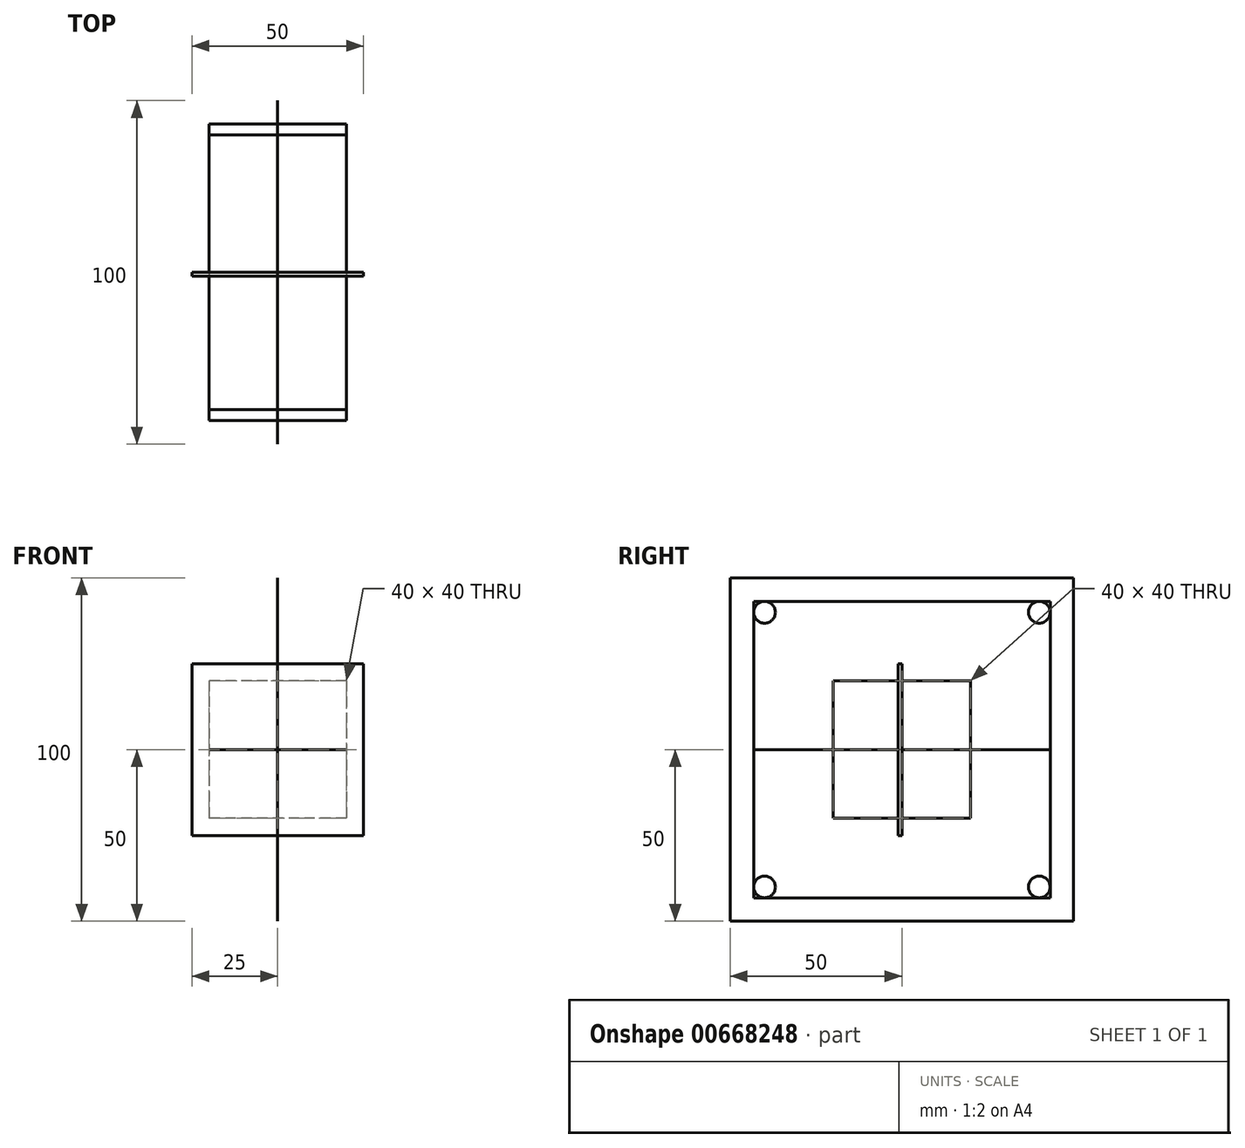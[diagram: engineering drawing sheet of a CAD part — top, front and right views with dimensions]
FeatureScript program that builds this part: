
annotation { "Feature Type Name" : "Feature", "Feature Type Description" : "" }
export const myFeature = defineFeature(function(context is Context, id is Id, definition is map)
    precondition{}
    {
        {
            var Q0;
            Q0=qCreatedBy(makeId("Front.planeOp"),FACE);
            var sketch = newSketch(context, id + "F0", { "sketchPlane" : qUnion([Q0])});
            skLineSegment(sketch, "E0.bottom", {"start": v(25, 25) * mm, "end": v(-25, 25) * mm});
            skLineSegment(sketch, "E0.top", {"start": v(25, -25) * mm, "end": v(-25, -25) * mm});
            skLineSegment(sketch, "E0.left", {"start": v(25, 25) * mm, "end": v(25, -25) * mm});
            skLineSegment(sketch, "E0.right", {"start": v(-25, 25) * mm, "end": v(-25, -25) * mm});
            skPoint(sketch, "E0.middle", {"position": v(0, 0) * mm});
            skLineSegment(sketch, "E1.bottom", {"start": v(20, 20) * mm, "end": v(-20, 20) * mm});
            skLineSegment(sketch, "E1.top", {"start": v(20, -20) * mm, "end": v(-20, -20) * mm});
            skLineSegment(sketch, "E1.left", {"start": v(20, 20) * mm, "end": v(20, -20) * mm});
            skLineSegment(sketch, "E1.right", {"start": v(-20, 20) * mm, "end": v(-20, -20) * mm});
            skSolve(sketch);
        }
        {
            var Q0;
            Q0=makeQuery(id+"F0.imprint","IMPRINT",FACE,{"disambiguationData":[TD([[makeQuery(id+"F0.imprint","IMPRINT",EDGE,{"derivedFrom":sQuery(id+"F0.wireOp",EDGE,"E0.bottom")}),1.0]])]});
            extrude(context, id + "F1", {"entities" : qUnion([Q0]), "depth" : 1 / 406.4 * mm, "offsetDistance" : 25.4 * mm});
        }
        {
            var Q0;
            Q0=qCreatedBy(makeId("Right.planeOp"),FACE);
            var sketch = newSketch(context, id + "F2", { "sketchPlane" : qUnion([Q0])});
            skLineSegment(sketch, "E2.bottom", {"start": v(-20, 20) * mm, "end": v(20, 20) * mm});
            skLineSegment(sketch, "E2.top", {"start": v(-20, -20) * mm, "end": v(20, -20) * mm});
            skLineSegment(sketch, "E2.left", {"start": v(-20, 20) * mm, "end": v(-20, -20) * mm});
            skLineSegment(sketch, "E2.right", {"start": v(20, 20) * mm, "end": v(20, -20) * mm});
            skPoint(sketch, "E2.middle", {"position": v(0, 0) * mm});
            skLineSegment(sketch, "E3.bottom", {"start": v(-50, 50) * mm, "end": v(50, 50) * mm});
            skLineSegment(sketch, "E3.top", {"start": v(-50, -50) * mm, "end": v(50, -50) * mm});
            skLineSegment(sketch, "E3.left", {"start": v(-50, 50) * mm, "end": v(-50, -50) * mm});
            skLineSegment(sketch, "E3.right", {"start": v(50, 50) * mm, "end": v(50, -50) * mm});
            skCircle(sketch, "E4", {"center": v(-40, 40) * mm, "radius": 3.18 * mm});
            skLineSegment(sketch, "E5", {"start": v(-20, 20) * mm, "end": v(-50, 50) * mm, "construction": true});
            skCircle(sketch, "E6.1.0", {"center": v(-40, -40) * mm, "radius": 3.18 * mm});
            skCircle(sketch, "E6.2.0", {"center": v(40, -40) * mm, "radius": 3.18 * mm});
            skCircle(sketch, "E6.3.0", {"center": v(40, 40) * mm, "radius": 3.18 * mm});
            skSolve(sketch);
        }
        {
            var Q0;
            Q0=makeQuery(id+"F2.imprint","IMPRINT",FACE,{"disambiguationData":[TD([[makeQuery(id+"F2.imprint","IMPRINT",EDGE,{"derivedFrom":sQuery(id+"F2.wireOp",EDGE,"E2.bottom")}),1.0]])]});
            extrude(context, id + "F3", {"entities" : qUnion([Q0]), "depth" : 1 / 203.2 * mm, "offsetDistance" : 25.4 * mm});
        }
        {
            var Q0;
            Q0=qCreatedBy(makeId("Top.planeOp"),FACE);
            var sketch = newSketch(context, id + "F4", { "sketchPlane" : qUnion([Q0])});
            skLineSegment(sketch, "E7.bottom", {"start": v(20, 40) * mm, "end": v(-20, 40) * mm});
            skLineSegment(sketch, "E7.top", {"start": v(20, -40) * mm, "end": v(-20, -40) * mm});
            skLineSegment(sketch, "E7.left", {"start": v(20, 40) * mm, "end": v(20, -40) * mm});
            skLineSegment(sketch, "E7.right", {"start": v(-20, 40) * mm, "end": v(-20, -40) * mm});
            skPoint(sketch, "E7.middle", {"position": v(0, 0) * mm});
            skSolve(sketch);
        }
        {
            var Q0;
            Q0=makeQuery(id+"F4.imprint","IMPRINT",FACE,{"disambiguationData":[TD([[makeQuery(id+"F4.imprint","IMPRINT",EDGE,{"derivedFrom":sQuery(id+"F4.wireOp",EDGE,"E7.bottom")}),1.0]])]});
            extrude(context, id + "F5", {"entities" : qUnion([Q0]), "depth" : 1 / 203.2 * mm, "offsetDistance" : 25 * mm});
        }
        {
            var Q0;
            Q0=qCreatedBy(makeId("Front.planeOp"),FACE);
            var sketch = newSketch(context, id + "F6", { "sketchPlane" : qUnion([Q0])});
            skLineSegment(sketch, "E8.bottom", {"start": v(25, 25) * mm, "end": v(-25, 25) * mm});
            skLineSegment(sketch, "E8.top", {"start": v(25, -25) * mm, "end": v(-25, -25) * mm});
            skLineSegment(sketch, "E8.left", {"start": v(25, 25) * mm, "end": v(25, -25) * mm});
            skLineSegment(sketch, "E8.right", {"start": v(-25, 25) * mm, "end": v(-25, -25) * mm});
            skPoint(sketch, "E8.middle", {"position": v(0, 0) * mm});
            skSolve(sketch);
        }
        {
            var Q0;
            Q0 = qSketchRegion(id + "F6", true);
            extrude(context, id + "F7", {"entities" : qUnion([Q0]), "depth" : 1.1 * mm, "offsetDistance" : 25 * mm});
        }
        {
            var Q0;
            Q0=qCreatedBy(makeId("Top.planeOp"),FACE);
            var sketch = newSketch(context, id + "F8", { "sketchPlane" : qUnion([Q0])});
            skLineSegment(sketch, "E9.bottom", {"start": v(-20, 43.18) * mm, "end": v(20, 43.18) * mm});
            skLineSegment(sketch, "E9.top", {"start": v(-20, -43.17) * mm, "end": v(20, -43.17) * mm});
            skLineSegment(sketch, "E9.left", {"start": v(-20, 43.18) * mm, "end": v(-20, -43.17) * mm});
            skLineSegment(sketch, "E9.right", {"start": v(20, 43.18) * mm, "end": v(20, -43.17) * mm});
            skPoint(sketch, "E9.middle", {"position": v(0, 0) * mm});
            skSolve(sketch);
        }
        {
            var Q0;
            Q0 = qSketchRegion(id + "F8", true);
            extrude(context, id + "F9", {"entities" : qUnion([Q0]), "depth" : 1 / 203.2 * mm, "offsetDistance" : 25 * mm});
        }
        {
            var Q0;
            Q0=qCreatedBy(makeId("Right.planeOp"),FACE);
            var sketch = newSketch(context, id + "F10", { "sketchPlane" : qUnion([Q0])});
            skLineSegment(sketch, "E10.bottom", {"start": v(43.17, 43.17) * mm, "end": v(-43.18, 43.17) * mm});
            skLineSegment(sketch, "E10.top", {"start": v(43.17, -43.17) * mm, "end": v(-43.18, -43.17) * mm});
            skLineSegment(sketch, "E10.left", {"start": v(43.17, 43.17) * mm, "end": v(43.17, -43.17) * mm});
            skLineSegment(sketch, "E10.right", {"start": v(-43.18, 43.17) * mm, "end": v(-43.18, -43.17) * mm});
            skPoint(sketch, "E10.middle", {"position": v(0, 0) * mm});
            skSolve(sketch);
        }
        {
            var Q0;
            Q0 = qSketchRegion(id + "F10", true);
            extrude(context, id + "F11", {"entities" : qUnion([Q0]), "depth" : 1 / 203.2 * mm, "offsetDistance" : 25 * mm});
        }
    });
